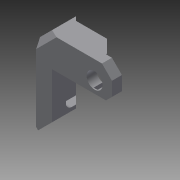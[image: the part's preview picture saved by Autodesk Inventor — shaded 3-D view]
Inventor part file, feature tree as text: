
AUTODESK INVENTOR PART (.ipt)
format: ipt  version: 2015 (Build 190159000, 159)  size: 133,632 bytes
history: native  units: mm
features: sketch x8, other x3
ambient origin geometry x8: Origin, YZ Plane, XZ Plane, XY Plane, X Axis, Y Axis, Z Axis, Center Point
bodies: Solid1 (feature_tree)
feature tree (11):
  other  "z-axis-top.ipt"
  other  "Solid1::z-axis-top.ipt"
  other  "TaggingFeature1"
  sketch  "Sketch1"  dims[d0=10.0mm]
  sketch  "Sketch2"
  sketch  "Sketch3"
  sketch  "Sketch4"
  sketch  "Sketch5"
  sketch  "Sketch6"
  sketch  "Sketch7"
  sketch  "Sketch8"
